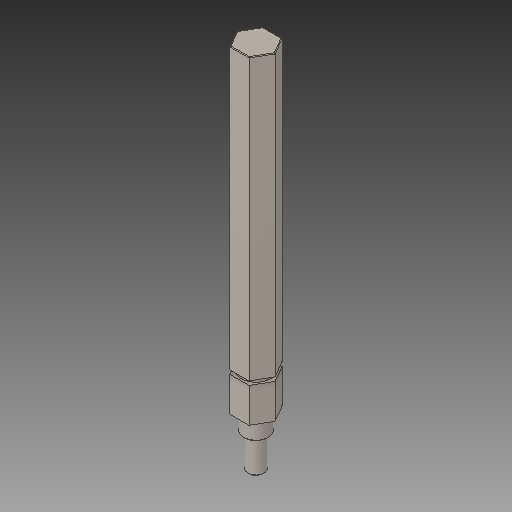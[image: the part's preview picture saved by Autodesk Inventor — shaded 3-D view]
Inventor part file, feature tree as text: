
AUTODESK INVENTOR PART (.ipt)
format: ipt  version: 2019 (Build 230136000, 136)  size: 99,328 bytes
history: native  units: in
note: dims shown in document units (in); Inventor stores cm internally (conversion verified against a paired STEP export)
features: chamfer x1
ambient origin geometry x8: Origin, YZ Plane, XZ Plane, XY Plane, X Axis, Y Axis, Z Axis, Center Point
bodies: Solid1 (feature_tree)
feature tree (1):
  chamfer  "Chamfer1"  [1 undecoded]
note: 1 required parameter value undecoded (feature->parameter linkage not recoverable at this tier; creation-order binding heuristic only, values carry confidence <= 0.55)
